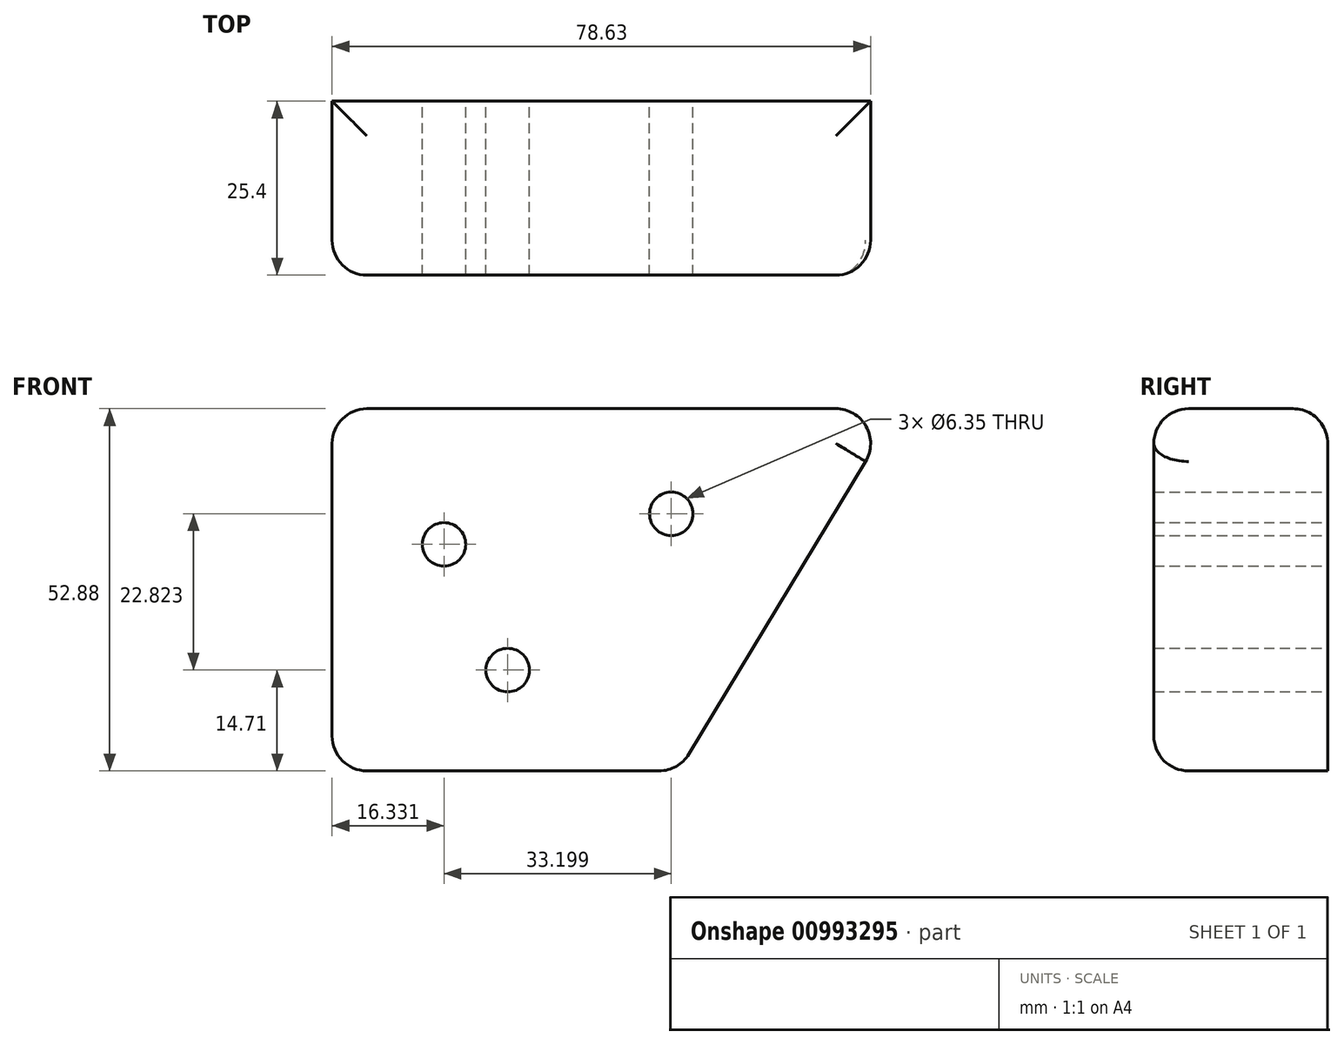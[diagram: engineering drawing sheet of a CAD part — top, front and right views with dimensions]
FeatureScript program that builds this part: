
annotation { "Feature Type Name" : "Feature", "Feature Type Description" : "" }
export const myFeature = defineFeature(function(context is Context, id is Id, definition is map)
    precondition{}
    {
        {
            var Q0;
            Q0=qCreatedBy(makeId("Front.planeOp"),FACE);
            var sketch = newSketch(context, id + "F0", { "sketchPlane" : qUnion([Q0])});
            skLineSegment(sketch, "E0.top", {"start": v(33.02, 38.17) * mm, "end": v(-49.53, 38.17) * mm});
            skLineSegment(sketch, "E0.right", {"start": v(-49.53, -14.7) * mm, "end": v(-49.53, 38.17) * mm});
            skLineSegment(sketch, "E1", {"start": v(60.49, 83.63) * mm, "end": v(60.49, 83.63) * mm});
            skLineSegment(sketch, "E2", {"start": v(33.02, 38.17) * mm, "end": v(1.08, -14.7) * mm});
            skLineSegment(sketch, "E3.trimOffspring", {"start": v(1.08, -14.7) * mm, "end": v(-49.53, -14.7) * mm});
            skSolve(sketch);
        }
        {
            var Q0;
            Q0 = qSketchRegion(id + "F0", true);
            var sketch = newSketch(context, id + "F1", { "sketchPlane" : qUnion([Q0])});
            skSolve(sketch);
        }
        {
            var Q0;
            Q0=makeQuery(id+"F1.imprint","IMPRINT",FACE,{"disambiguationData":[TD([[makeQuery(id+"F1.imprint","IMPRINT",EDGE,{"derivedFrom":makeQuery(id+"F0.imprint","IMPRINT",EDGE,{"derivedFrom":sQuery(id+"F0.wireOp",EDGE,"E0.top")})}),1.0]])]});
            extrude(context, id + "F2", {"entities" : qUnion([Q0]), "depth" : 25.4 * mm, "offsetDistance" : 25.4 * mm});
        }
        {
            var Q0;
            Q0=makeQuery(id+"F2.opExtrude","SWEPT_FACE",FACE,{"disambiguationData":[OSD([sQuery(id+"F0.wireOp",EDGE,"E0.top")])]});
            fillet(context, id + "F3", {"entities" : qUnion([Q0]), "radius" : 5.08 * mm, "tangentPropagation" : true, "allowEdgeOverflow" : false});
        }
        {
            var Q0;
            Q0=makeQuery(id+"F2.opExtrude","SWEPT_EDGE",EDGE,{"disambiguationData":[OSD([sQuery(id+"F0.wireOp",EDGE,"E2"),sQuery(id+"F0.wireOp",EDGE,"E3.trimOffspring")])]});
            var Q1;
            Q1=makeQuery(id+"F2.opExtrude","SWEPT_EDGE",EDGE,{"disambiguationData":[OSD([sQuery(id+"F0.wireOp",EDGE,"E0.right"),sQuery(id+"F0.wireOp",EDGE,"E3.trimOffspring")])]});
            fillet(context, id + "F4", {"entities" : qUnion([Q0, Q1]), "radius" : 5.08 * mm, "tangentPropagation" : true, "allowEdgeOverflow" : false});
        }
        {
            var Q0;
            Q0=makeQuery(id+"F2.opExtrude","CAP_EDGE",EDGE,{"disambiguationData":[OSD([sQuery(id+"F0.wireOp",EDGE,"E0.right")])],"isStart":false});
            var Q1;
            {var subQ0=sQuery(id+"F0.wireOp",EDGE,"E3.trimOffspring");var subQ1=sQuery(id+"F0.wireOp",EDGE,"E0.right");Q1=makeQuery(id+"F4.opFillet","BLEND_EDGE",EDGE,{"blendedFrom":[makeQuery(id+"F2.opExtrude","SWEPT_EDGE",EDGE,{"disambiguationData":[OSD([subQ1,subQ0])]}),makeQuery(id+"F2.opExtrude","CAP_FACE",FACE,{"disambiguationData":[OSD([sQuery(id+"F0.wireOp",EDGE,"E0.top"),subQ1,sQuery(id+"F0.wireOp",EDGE,"E2"),subQ0])],"isStart":false})],"blendedInto":[makeQuery(id+"F2.opExtrude","CAP_FACE",FACE,{"disambiguationData":[OSD([sQuery(id+"F0.wireOp",EDGE,"E0.top"),subQ1,sQuery(id+"F0.wireOp",EDGE,"E2"),subQ0])],"isStart":false})]});}
            var Q2;
            Q2=makeQuery(id+"F2.opExtrude","CAP_EDGE",EDGE,{"disambiguationData":[OSD([sQuery(id+"F0.wireOp",EDGE,"E3.trimOffspring")])],"isStart":false});
            var Q3;
            {var subQ0=sQuery(id+"F0.wireOp",EDGE,"E3.trimOffspring");var subQ1=sQuery(id+"F0.wireOp",EDGE,"E2");Q3=makeQuery(id+"F4.opFillet","BLEND_EDGE",EDGE,{"blendedFrom":[makeQuery(id+"F2.opExtrude","SWEPT_EDGE",EDGE,{"disambiguationData":[OSD([subQ1,subQ0])]}),makeQuery(id+"F2.opExtrude","CAP_FACE",FACE,{"disambiguationData":[OSD([sQuery(id+"F0.wireOp",EDGE,"E0.top"),sQuery(id+"F0.wireOp",EDGE,"E0.right"),subQ1,subQ0])],"isStart":false})],"blendedInto":[makeQuery(id+"F2.opExtrude","CAP_FACE",FACE,{"disambiguationData":[OSD([sQuery(id+"F0.wireOp",EDGE,"E0.top"),sQuery(id+"F0.wireOp",EDGE,"E0.right"),subQ1,subQ0])],"isStart":false})]});}
            var Q4;
            Q4=makeQuery(id+"F2.opExtrude","CAP_EDGE",EDGE,{"disambiguationData":[OSD([sQuery(id+"F0.wireOp",EDGE,"E2")])],"isStart":false});
            var Q5;
            {var subQ0=sQuery(id+"F0.wireOp",EDGE,"E2");var subQ1=sQuery(id+"F0.wireOp",EDGE,"E0.top");Q5=makeQuery(id+"F3.opFillet","BLEND_EDGE",EDGE,{"blendedFrom":[makeQuery(id+"F2.opExtrude","SWEPT_EDGE",EDGE,{"disambiguationData":[OSD([subQ1,subQ0])]}),makeQuery(id+"F2.opExtrude","CAP_FACE",FACE,{"disambiguationData":[OSD([subQ1,sQuery(id+"F0.wireOp",EDGE,"E0.right"),subQ0,sQuery(id+"F0.wireOp",EDGE,"E3.trimOffspring")])],"isStart":false})],"blendedInto":[makeQuery(id+"F2.opExtrude","CAP_FACE",FACE,{"disambiguationData":[OSD([subQ1,sQuery(id+"F0.wireOp",EDGE,"E0.right"),subQ0,sQuery(id+"F0.wireOp",EDGE,"E3.trimOffspring")])],"isStart":false})]});}
            var Q6;
            {var subQ0=sQuery(id+"F0.wireOp",EDGE,"E0.top");Q6=makeQuery(id+"F3.opFillet","BLEND_EDGE",EDGE,{"blendedFrom":[makeQuery(id+"F2.opExtrude","SWEPT_EDGE",EDGE,{"disambiguationData":[OSD([subQ0,sQuery(id+"F0.wireOp",EDGE,"E2")])]}),makeQuery(id+"F2.opExtrude","CAP_EDGE",EDGE,{"disambiguationData":[OSD([subQ0])],"isStart":false})],"blendedInto":[]});}
            fillet(context, id + "F5", {"entities" : qUnion([Q0, Q1, Q2, Q3, Q4, Q5, Q6]), "radius" : 5.08 * mm, "tangentPropagation" : true, "allowEdgeOverflow" : false});
        }
        {
            var Q0;
            Q0=qCreatedBy(makeId("Front.planeOp"),FACE);
            var sketch = newSketch(context, id + "F6", { "sketchPlane" : qUnion([Q0])});
            skPoint(sketch, "E4", {"position": v(-33.2, 18.36) * mm});
            skPoint(sketch, "E5", {"position": v(-23.89, 0) * mm});
            skPoint(sketch, "E6", {"position": v(0, 22.82) * mm});
            skSolve(sketch);
        }
        {
            var Q0;
            Q0=sQuery(id+"F6.wireOp",VERTEX,"E5");
            var Q1;
            Q1=sQuery(id+"F6.wireOp",VERTEX,"E4");
            var Q2;
            Q2=sQuery(id+"F6.wireOp",VERTEX,"E6");
            var Q3;
            Q3=makeQuery(id+"F2.opExtrude","SWEPT_BODY",BODY,{"disambiguationData":[OSD([sQuery(id+"F0.wireOp",EDGE,"E0.top"),sQuery(id+"F0.wireOp",EDGE,"E0.right"),sQuery(id+"F0.wireOp",EDGE,"E2"),sQuery(id+"F0.wireOp",EDGE,"E3.trimOffspring")])]});
            hole(context, id + "F7", {"style" : HoleStyle.SIMPLE, "endStyle" : HoleEndStyle.THROUGH, "oppositeDirection" : true, "holeDiameter" : 6.35 * mm, "majorDiameter" : 6.35 * mm, "isTappedThrough" : true, "tappedDepth" : 12.7 * mm, "tapClearance" : 3, "locations" : qUnion([Q0, Q1, Q2]), "scope" : qUnion([Q3])});
        }
    });
